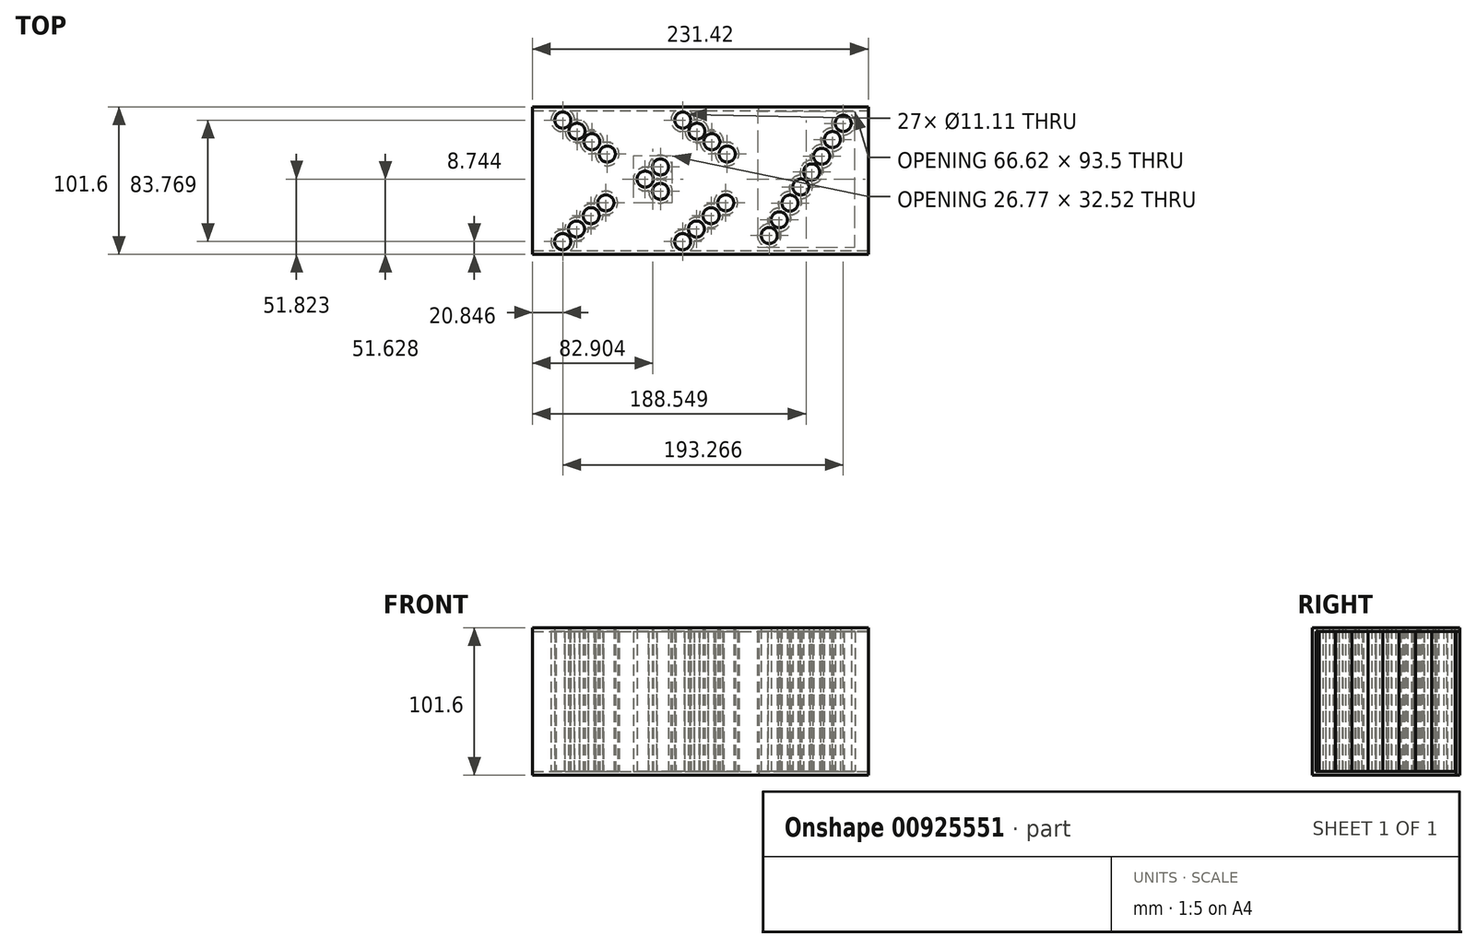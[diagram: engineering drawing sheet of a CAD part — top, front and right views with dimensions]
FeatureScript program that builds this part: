
annotation { "Feature Type Name" : "Feature", "Feature Type Description" : "" }
export const myFeature = defineFeature(function(context is Context, id is Id, definition is map)
    precondition{}
    {
        {
            var Q0;
            Q0=qCreatedBy(makeId("Top.planeOp"),FACE);
            var sketch = newSketch(context, id + "F0", { "sketchPlane" : qUnion([Q0])});
            skLineSegment(sketch, "E0.bottom", {"start": v(-106.7, 29.56) * mm, "end": v(124.73, 29.56) * mm});
            skLineSegment(sketch, "E0.top", {"start": v(-106.7, -72.04) * mm, "end": v(124.73, -72.04) * mm});
            skLineSegment(sketch, "E0.left", {"start": v(-106.7, 29.56) * mm, "end": v(-106.7, -72.04) * mm});
            skLineSegment(sketch, "E0.right", {"start": v(124.73, 29.56) * mm, "end": v(124.73, -72.04) * mm});
            skCircle(sketch, "E1", {"center": v(-85.84, -63.3) * mm, "radius": 5.55 * mm});
            skCircle(sketch, "E2", {"center": v(-76.34, -54.61) * mm, "radius": 5.55 * mm});
            skCircle(sketch, "E3", {"center": v(-66.26, -45.42) * mm, "radius": 5.55 * mm});
            skCircle(sketch, "E4", {"center": v(-56.15, -36.56) * mm, "radius": 5.55 * mm});
            skCircle(sketch, "E5", {"center": v(-85.77, 20.47) * mm, "radius": 5.55 * mm});
            skCircle(sketch, "E6", {"center": v(-76.04, 12.8) * mm, "radius": 5.55 * mm});
            skCircle(sketch, "E7", {"center": v(-65.76, 5.55) * mm, "radius": 5.55 * mm});
            skCircle(sketch, "E8", {"center": v(-55.18, -2.91) * mm, "radius": 5.55 * mm});
            skCircle(sketch, "E9", {"center": v(-29.07, -20.18) * mm, "radius": 5.55 * mm});
            skCircle(sketch, "E10", {"center": v(-18.5, -28.65) * mm, "radius": 5.55 * mm});
            skCircle(sketch, "E11", {"center": v(-18.5, -11.78) * mm, "radius": 5.55 * mm});
            skCircle(sketch, "E12", {"center": v(-3.22, -63.3) * mm, "radius": 5.55 * mm});
            skCircle(sketch, "E13", {"center": v(6.28, -54.61) * mm, "radius": 5.55 * mm});
            skCircle(sketch, "E14", {"center": v(16.36, -45.42) * mm, "radius": 5.55 * mm});
            skCircle(sketch, "E15", {"center": v(26.47, -36.56) * mm, "radius": 5.55 * mm});
            skCircle(sketch, "E16", {"center": v(-3.15, 20.47) * mm, "radius": 5.55 * mm});
            skCircle(sketch, "E17", {"center": v(6.58, 12.8) * mm, "radius": 5.55 * mm});
            skCircle(sketch, "E18", {"center": v(16.86, 5.55) * mm, "radius": 5.55 * mm});
            skCircle(sketch, "E19", {"center": v(27.44, -2.91) * mm, "radius": 5.55 * mm});
            skCircle(sketch, "E20", {"center": v(56.4, -59.08) * mm, "radius": 5.55 * mm});
            skCircle(sketch, "E21", {"center": v(63.34, -48.23) * mm, "radius": 5.55 * mm});
            skCircle(sketch, "E22", {"center": v(70.7, -36.74) * mm, "radius": 5.55 * mm});
            skCircle(sketch, "E23", {"center": v(78.17, -25.57) * mm, "radius": 5.55 * mm});
            skCircle(sketch, "E24", {"center": v(85.66, -15.26) * mm, "radius": 5.55 * mm});
            skCircle(sketch, "E25", {"center": v(92.59, -4.4) * mm, "radius": 5.55 * mm});
            skCircle(sketch, "E26", {"center": v(99.95, 7.08) * mm, "radius": 5.55 * mm});
            skCircle(sketch, "E27", {"center": v(107.42, 18.25) * mm, "radius": 5.55 * mm});
            skSolve(sketch);
        }
        {
            var Q0;
            Q0=makeQuery(id+"F0.imprint","IMPRINT",FACE,{"disambiguationData":[TD([[makeQuery(id+"F0.imprint","IMPRINT",EDGE,{"derivedFrom":sQuery(id+"F0.wireOp",EDGE,"E5")}),1.0]])]});
            var Q1;
            Q1=makeQuery(id+"F0.imprint","IMPRINT",FACE,{"disambiguationData":[TD([[makeQuery(id+"F0.imprint","IMPRINT",EDGE,{"derivedFrom":sQuery(id+"F0.wireOp",EDGE,"E6")}),1.0]])]});
            var Q2;
            Q2=makeQuery(id+"F0.imprint","IMPRINT",FACE,{"disambiguationData":[TD([[makeQuery(id+"F0.imprint","IMPRINT",EDGE,{"derivedFrom":sQuery(id+"F0.wireOp",EDGE,"E7")}),1.0]])]});
            var Q3;
            Q3=makeQuery(id+"F0.imprint","IMPRINT",FACE,{"disambiguationData":[TD([[makeQuery(id+"F0.imprint","IMPRINT",EDGE,{"derivedFrom":sQuery(id+"F0.wireOp",EDGE,"E8")}),1.0]])]});
            var Q4;
            Q4=makeQuery(id+"F0.imprint","IMPRINT",FACE,{"disambiguationData":[TD([[makeQuery(id+"F0.imprint","IMPRINT",EDGE,{"derivedFrom":sQuery(id+"F0.wireOp",EDGE,"E1")}),1.0]])]});
            var Q5;
            Q5=makeQuery(id+"F0.imprint","IMPRINT",FACE,{"disambiguationData":[TD([[makeQuery(id+"F0.imprint","IMPRINT",EDGE,{"derivedFrom":sQuery(id+"F0.wireOp",EDGE,"E2")}),1.0]])]});
            var Q6;
            Q6=makeQuery(id+"F0.imprint","IMPRINT",FACE,{"disambiguationData":[TD([[makeQuery(id+"F0.imprint","IMPRINT",EDGE,{"derivedFrom":sQuery(id+"F0.wireOp",EDGE,"E3")}),1.0]])]});
            var Q7;
            Q7=makeQuery(id+"F0.imprint","IMPRINT",FACE,{"disambiguationData":[TD([[makeQuery(id+"F0.imprint","IMPRINT",EDGE,{"derivedFrom":sQuery(id+"F0.wireOp",EDGE,"E4")}),1.0]])]});
            var Q8;
            Q8=makeQuery(id+"F0.imprint","IMPRINT",FACE,{"disambiguationData":[TD([[makeQuery(id+"F0.imprint","IMPRINT",EDGE,{"derivedFrom":sQuery(id+"F0.wireOp",EDGE,"E9")}),1.0]])]});
            var Q9;
            Q9=makeQuery(id+"F0.imprint","IMPRINT",FACE,{"disambiguationData":[TD([[makeQuery(id+"F0.imprint","IMPRINT",EDGE,{"derivedFrom":sQuery(id+"F0.wireOp",EDGE,"E11")}),1.0]])]});
            var Q10;
            Q10=makeQuery(id+"F0.imprint","IMPRINT",FACE,{"disambiguationData":[TD([[makeQuery(id+"F0.imprint","IMPRINT",EDGE,{"derivedFrom":sQuery(id+"F0.wireOp",EDGE,"E10")}),1.0]])]});
            var Q11;
            Q11=makeQuery(id+"F0.imprint","IMPRINT",FACE,{"disambiguationData":[TD([[makeQuery(id+"F0.imprint","IMPRINT",EDGE,{"derivedFrom":sQuery(id+"F0.wireOp",EDGE,"E12")}),1.0]])]});
            var Q12;
            Q12=makeQuery(id+"F0.imprint","IMPRINT",FACE,{"disambiguationData":[TD([[makeQuery(id+"F0.imprint","IMPRINT",EDGE,{"derivedFrom":sQuery(id+"F0.wireOp",EDGE,"E13")}),1.0]])]});
            var Q13;
            Q13=makeQuery(id+"F0.imprint","IMPRINT",FACE,{"disambiguationData":[TD([[makeQuery(id+"F0.imprint","IMPRINT",EDGE,{"derivedFrom":sQuery(id+"F0.wireOp",EDGE,"E14")}),1.0]])]});
            var Q14;
            Q14=makeQuery(id+"F0.imprint","IMPRINT",FACE,{"disambiguationData":[TD([[makeQuery(id+"F0.imprint","IMPRINT",EDGE,{"derivedFrom":sQuery(id+"F0.wireOp",EDGE,"E15")}),1.0]])]});
            var Q15;
            Q15=makeQuery(id+"F0.imprint","IMPRINT",FACE,{"disambiguationData":[TD([[makeQuery(id+"F0.imprint","IMPRINT",EDGE,{"derivedFrom":sQuery(id+"F0.wireOp",EDGE,"E19")}),1.0]])]});
            var Q16;
            Q16=makeQuery(id+"F0.imprint","IMPRINT",FACE,{"disambiguationData":[TD([[makeQuery(id+"F0.imprint","IMPRINT",EDGE,{"derivedFrom":sQuery(id+"F0.wireOp",EDGE,"E18")}),1.0]])]});
            var Q17;
            Q17=makeQuery(id+"F0.imprint","IMPRINT",FACE,{"disambiguationData":[TD([[makeQuery(id+"F0.imprint","IMPRINT",EDGE,{"derivedFrom":sQuery(id+"F0.wireOp",EDGE,"E17")}),1.0]])]});
            var Q18;
            Q18=makeQuery(id+"F0.imprint","IMPRINT",FACE,{"disambiguationData":[TD([[makeQuery(id+"F0.imprint","IMPRINT",EDGE,{"derivedFrom":sQuery(id+"F0.wireOp",EDGE,"E16")}),1.0]])]});
            var Q19;
            Q19=makeQuery(id+"F0.imprint","IMPRINT",FACE,{"disambiguationData":[TD([[makeQuery(id+"F0.imprint","IMPRINT",EDGE,{"derivedFrom":sQuery(id+"F0.wireOp",EDGE,"E20")}),1.0]])]});
            var Q20;
            Q20=makeQuery(id+"F0.imprint","IMPRINT",FACE,{"disambiguationData":[TD([[makeQuery(id+"F0.imprint","IMPRINT",EDGE,{"derivedFrom":sQuery(id+"F0.wireOp",EDGE,"E21")}),1.0]])]});
            var Q21;
            Q21=makeQuery(id+"F0.imprint","IMPRINT",FACE,{"disambiguationData":[TD([[makeQuery(id+"F0.imprint","IMPRINT",EDGE,{"derivedFrom":sQuery(id+"F0.wireOp",EDGE,"E22")}),1.0]])]});
            var Q22;
            Q22=makeQuery(id+"F0.imprint","IMPRINT",FACE,{"disambiguationData":[TD([[makeQuery(id+"F0.imprint","IMPRINT",EDGE,{"derivedFrom":sQuery(id+"F0.wireOp",EDGE,"E23")}),1.0]])]});
            var Q23;
            Q23=makeQuery(id+"F0.imprint","IMPRINT",FACE,{"disambiguationData":[TD([[makeQuery(id+"F0.imprint","IMPRINT",EDGE,{"derivedFrom":sQuery(id+"F0.wireOp",EDGE,"E24")}),1.0]])]});
            var Q24;
            Q24=makeQuery(id+"F0.imprint","IMPRINT",FACE,{"disambiguationData":[TD([[makeQuery(id+"F0.imprint","IMPRINT",EDGE,{"derivedFrom":sQuery(id+"F0.wireOp",EDGE,"E25")}),1.0]])]});
            var Q25;
            Q25=makeQuery(id+"F0.imprint","IMPRINT",FACE,{"disambiguationData":[TD([[makeQuery(id+"F0.imprint","IMPRINT",EDGE,{"derivedFrom":sQuery(id+"F0.wireOp",EDGE,"E26")}),1.0]])]});
            var Q26;
            Q26=makeQuery(id+"F0.imprint","IMPRINT",FACE,{"disambiguationData":[TD([[makeQuery(id+"F0.imprint","IMPRINT",EDGE,{"derivedFrom":sQuery(id+"F0.wireOp",EDGE,"E27")}),1.0]])]});
            extrude(context, id + "F1", {"entities" : qUnion([Q0, Q1, Q2, Q3, Q4, Q5, Q6, Q7, Q8, Q9, Q10, Q11, Q12, Q13, Q14, Q15, Q16, Q17, Q18, Q19, Q20, Q21, Q22, Q23, Q24, Q25, Q26]), "depth" : 101.6 * mm, "offsetDistance" : 25.4 * mm});
        }
        {
            var Q0;
            Q0=makeQuery(id+"F0.imprint","IMPRINT",FACE,{"disambiguationData":[TD([[makeQuery(id+"F0.imprint","IMPRINT",EDGE,{"derivedFrom":sQuery(id+"F0.wireOp",EDGE,"E0.bottom")}),-1.0]])]});
            var sketch = newSketch(context, id + "F2", { "sketchPlane" : qUnion([Q0])});
            skLineSegment(sketch, "E28.0", {"start": v(-106.7, -72.04) * mm, "end": v(124.73, -72.04) * mm});
            skSolve(sketch);
        }
        {
            var Q0;
            Q0 = qSketchRegion(id + "F2", true);
            var Q1;
            Q1=makeQuery(id+"F0.imprint","IMPRINT",FACE,{"disambiguationData":[TD([[makeQuery(id+"F0.imprint","IMPRINT",EDGE,{"derivedFrom":sQuery(id+"F0.wireOp",EDGE,"E0.bottom")}),-1.0]])]});
            extrude(context, id + "F3", {"entities" : qUnion([Q0, Q1]), "depth" : 101.6 * mm, "offsetDistance" : 25.4 * mm});
        }
        {
            var Q0;
            Q0=makeQuery(id+"F3.opExtrude","SWEPT_FACE",FACE,{"disambiguationData":[OSD([sQuery(id+"F0.wireOp",EDGE,"E0.left")])]});
            var Q1;
            Q1=makeQuery(id+"F3.opExtrude","SWEPT_FACE",FACE,{"disambiguationData":[OSD([sQuery(id+"F0.wireOp",EDGE,"E0.right")])]});
            shell(context, id + "F4", {"entities" : qUnion([Q0, Q1]), "thickness" : 2.54 * mm});
        }
        {
            var Q0;
            Q0=makeQuery(id+"F3.opExtrude","SWEPT_FACE",FACE,{"disambiguationData":[OSD([sQuery(id+"F0.wireOp",EDGE,"E0.bottom")])]});
            var sketch = newSketch(context, id + "F5", { "sketchPlane" : qUnion([Q0])});
            skLineSegment(sketch, "E29.0", {"start": v(-124.73, 99.06) * mm, "end": v(-124.73, 2.54) * mm});
            skLineSegment(sketch, "E30.bottom", {"start": v(-124.73, 99.06) * mm, "end": v(-49.33, 99.06) * mm});
            skLineSegment(sketch, "E30.top", {"start": v(-124.73, 0) * mm, "end": v(-49.33, 0) * mm});
            skLineSegment(sketch, "E30.left", {"start": v(-124.73, 99.06) * mm, "end": v(-124.73, 0) * mm});
            skLineSegment(sketch, "E30.right", {"start": v(-49.33, 99.06) * mm, "end": v(-49.33, 0) * mm});
            skSolve(sketch);
        }
        {
            var Q0;
            {var subQ0=sQuery(id+"F5.wireOp",EDGE,"E30.bottom");Q0=makeQuery(id+"F5.imprint","IMPRINT",FACE,{"disambiguationData":[TD([[makeQuery(id+"F5.imprint","IMPRINT",EDGE,{"derivedFrom":subQ0}),-1.0]])]});}
            extrude(context, id + "F6", {"entities" : qUnion([Q0]), "operationType" : NewBodyOperationType.REMOVE, "oppositeDirection" : true, "depth" : 2.54 * mm, "offsetDistance" : 25.4 * mm});
        }
    });
